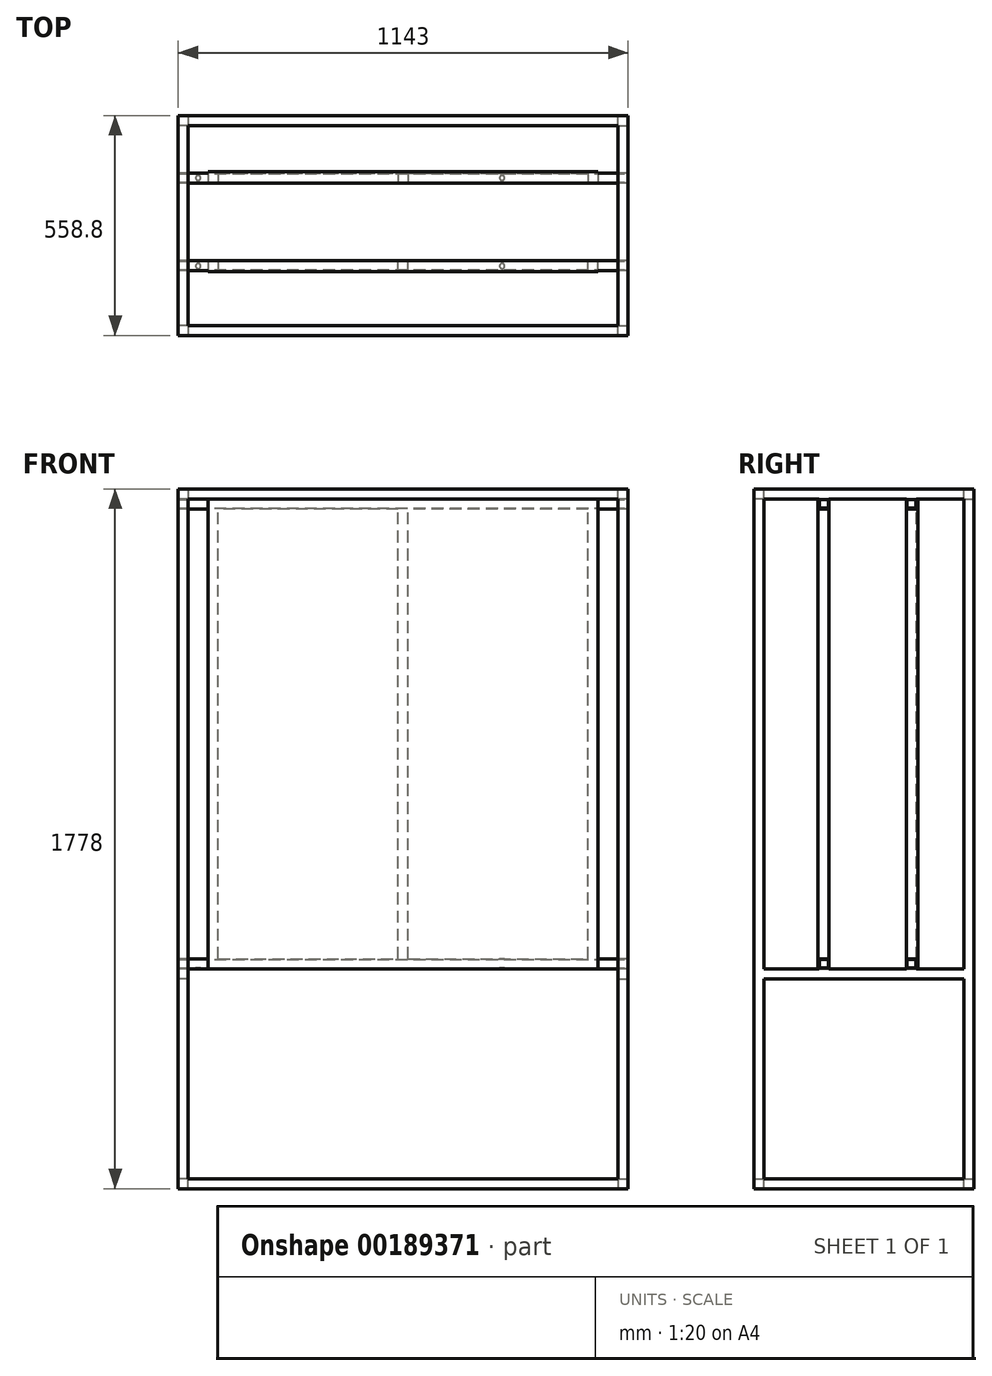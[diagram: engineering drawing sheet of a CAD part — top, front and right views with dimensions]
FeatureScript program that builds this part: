
annotation { "Feature Type Name" : "Feature", "Feature Type Description" : "" }
export const myFeature = defineFeature(function(context is Context, id is Id, definition is map)
    precondition{}
    {
        {
            var Q0;
            Q0=qCreatedBy(makeId("Front.planeOp"),FACE);
            var sketch = newSketch(context, id + "F0", { "sketchPlane" : qUnion([Q0])});
            skLineSegment(sketch, "E0.bottom", {"start": v(0, 0) * mm, "end": v(25.4, 0) * mm});
            skLineSegment(sketch, "E0.top", {"start": v(0, 25.4) * mm, "end": v(25.4, 25.4) * mm});
            skLineSegment(sketch, "E0.left", {"start": v(0, 0) * mm, "end": v(0, 25.4) * mm});
            skLineSegment(sketch, "E0.right", {"start": v(25.4, 0) * mm, "end": v(25.4, 25.4) * mm});
            skLineSegment(sketch, "E1.bottom", {"start": v(0, 533.4) * mm, "end": v(25.4, 533.4) * mm});
            skLineSegment(sketch, "E1.top", {"start": v(0, 558.8) * mm, "end": v(25.4, 558.8) * mm});
            skLineSegment(sketch, "E1.left", {"start": v(0, 533.4) * mm, "end": v(0, 558.8) * mm});
            skLineSegment(sketch, "E1.right", {"start": v(25.4, 533.4) * mm, "end": v(25.4, 558.8) * mm});
            skLineSegment(sketch, "E2.bottom", {"start": v(0, 1752.6) * mm, "end": v(25.4, 1752.6) * mm});
            skLineSegment(sketch, "E2.top", {"start": v(0, 1778) * mm, "end": v(25.4, 1778) * mm});
            skLineSegment(sketch, "E2.left", {"start": v(0, 1752.6) * mm, "end": v(0, 1778) * mm});
            skLineSegment(sketch, "E2.right", {"start": v(25.4, 1752.6) * mm, "end": v(25.4, 1778) * mm});
            skLineSegment(sketch, "E3", {"start": v(0, 25.4) * mm, "end": v(0, 558.8) * mm, "construction": true});
            skLineSegment(sketch, "E4.bottom", {"start": v(1117.6, 1778) * mm, "end": v(1143, 1778) * mm});
            skLineSegment(sketch, "E4.top", {"start": v(1117.6, 1752.6) * mm, "end": v(1143, 1752.6) * mm});
            skLineSegment(sketch, "E4.left", {"start": v(1117.6, 1778) * mm, "end": v(1117.6, 1752.6) * mm});
            skLineSegment(sketch, "E4.right", {"start": v(1143, 1778) * mm, "end": v(1143, 1752.6) * mm});
            skLineSegment(sketch, "E5.bottom", {"start": v(1117.6, 558.8) * mm, "end": v(1143, 558.8) * mm});
            skLineSegment(sketch, "E5.top", {"start": v(1117.6, 533.4) * mm, "end": v(1143, 533.4) * mm});
            skLineSegment(sketch, "E5.left", {"start": v(1117.6, 558.8) * mm, "end": v(1117.6, 533.4) * mm});
            skLineSegment(sketch, "E5.right", {"start": v(1143, 558.8) * mm, "end": v(1143, 533.4) * mm});
            skLineSegment(sketch, "E6.bottom", {"start": v(1117.6, 25.4) * mm, "end": v(1143, 25.4) * mm});
            skLineSegment(sketch, "E6.top", {"start": v(1117.6, 0) * mm, "end": v(1143, 0) * mm});
            skLineSegment(sketch, "E6.left", {"start": v(1117.6, 25.4) * mm, "end": v(1117.6, 0) * mm});
            skLineSegment(sketch, "E6.right", {"start": v(1143, 25.4) * mm, "end": v(1143, 0) * mm});
            skSolve(sketch);
        }
        {
            var Q0;
            Q0=qSketchRegion(id+"F0",true);
            extrude(context, id + "F1", {"entities" : qUnion([Q0]), "depth" : 558.8 * mm});
        }
        {
            var Q0;
            Q0=qCreatedBy(makeId("Right.planeOp"),FACE);
            var sketch = newSketch(context, id + "F2", { "sketchPlane" : qUnion([Q0])});
            skLineSegment(sketch, "E7.bottom", {"start": v(-558.8, 1752.6) * mm, "end": v(-533.4, 1752.6) * mm});
            skLineSegment(sketch, "E7.top", {"start": v(-558.8, 1778) * mm, "end": v(-533.4, 1778) * mm});
            skLineSegment(sketch, "E7.left", {"start": v(-558.8, 1778) * mm, "end": v(-558.8, 1752.6) * mm});
            skLineSegment(sketch, "E7.right", {"start": v(-533.4, 1778) * mm, "end": v(-533.4, 1752.6) * mm});
            skLineSegment(sketch, "E8.bottom", {"start": v(0, 1752.6) * mm, "end": v(-25.4, 1752.6) * mm});
            skLineSegment(sketch, "E8.top", {"start": v(0, 1778) * mm, "end": v(-25.4, 1778) * mm});
            skLineSegment(sketch, "E8.left", {"start": v(-25.4, 1778) * mm, "end": v(-25.4, 1752.6) * mm});
            skLineSegment(sketch, "E8.right", {"start": v(0, 1778) * mm, "end": v(0, 1752.6) * mm});
            skLineSegment(sketch, "E9.bottom", {"start": v(-558.8, 0) * mm, "end": v(-533.4, 0) * mm});
            skLineSegment(sketch, "E9.top", {"start": v(-558.8, 25.4) * mm, "end": v(-533.4, 25.4) * mm});
            skLineSegment(sketch, "E9.left", {"start": v(-558.8, 0) * mm, "end": v(-558.8, 25.4) * mm});
            skLineSegment(sketch, "E9.right", {"start": v(-533.4, 0) * mm, "end": v(-533.4, 25.4) * mm});
            skLineSegment(sketch, "E10.bottom", {"start": v(0, 0) * mm, "end": v(-25.4, 0) * mm});
            skLineSegment(sketch, "E10.top", {"start": v(0, 25.4) * mm, "end": v(-25.4, 25.4) * mm});
            skLineSegment(sketch, "E10.left", {"start": v(-25.4, 0) * mm, "end": v(-25.4, 25.4) * mm});
            skLineSegment(sketch, "E10.right", {"start": v(0, 0) * mm, "end": v(0, 25.4) * mm});
            skLineSegment(sketch, "E11.bottom", {"start": v(-393.7, 1752.6) * mm, "end": v(-368.3, 1752.6) * mm});
            skLineSegment(sketch, "E11.top", {"start": v(-393.7, 1727.2) * mm, "end": v(-368.3, 1727.2) * mm});
            skLineSegment(sketch, "E11.left", {"start": v(-393.7, 1752.6) * mm, "end": v(-393.7, 1727.2) * mm});
            skLineSegment(sketch, "E11.right", {"start": v(-368.3, 1752.6) * mm, "end": v(-368.3, 1727.2) * mm});
            skLineSegment(sketch, "E12.bottom", {"start": v(-171.45, 1752.6) * mm, "end": v(-146.05, 1752.6) * mm});
            skLineSegment(sketch, "E12.top", {"start": v(-171.45, 1727.2) * mm, "end": v(-146.05, 1727.2) * mm});
            skLineSegment(sketch, "E12.left", {"start": v(-171.45, 1752.6) * mm, "end": v(-171.45, 1727.2) * mm});
            skLineSegment(sketch, "E12.right", {"start": v(-146.05, 1752.6) * mm, "end": v(-146.05, 1727.2) * mm});
            skLineSegment(sketch, "E13.bottom", {"start": v(-393.7, 584.2) * mm, "end": v(-368.3, 584.2) * mm});
            skLineSegment(sketch, "E13.top", {"start": v(-393.7, 558.8) * mm, "end": v(-368.3, 558.8) * mm});
            skLineSegment(sketch, "E13.left", {"start": v(-393.7, 584.2) * mm, "end": v(-393.7, 558.8) * mm});
            skLineSegment(sketch, "E13.right", {"start": v(-368.3, 584.2) * mm, "end": v(-368.3, 558.8) * mm});
            skLineSegment(sketch, "E14.bottom", {"start": v(-146.05, 558.8) * mm, "end": v(-171.45, 558.8) * mm});
            skLineSegment(sketch, "E14.top", {"start": v(-146.05, 584.2) * mm, "end": v(-171.45, 584.2) * mm});
            skLineSegment(sketch, "E14.left", {"start": v(-146.05, 558.8) * mm, "end": v(-146.05, 584.2) * mm});
            skLineSegment(sketch, "E14.right", {"start": v(-171.45, 558.8) * mm, "end": v(-171.45, 584.2) * mm});
            skSolve(sketch);
        }
        {
            var Q0;
            Q0=qSketchRegion(id+"F2",true);
            var Q1;
            Q1=makeQuery(id+"F1.opExtrude","SWEPT_FACE",FACE,{"disambiguationData":[OSD([sQuery(id+"F0.wireOp",EDGE,"E4.right")])]});
            extrude(context, id + "F3", {"entities" : qUnion([Q0]), "operationType" : NewBodyOperationType.ADD, "endBound" : BoundingType.UP_TO_SURFACE, "endBoundEntityFace" : qUnion([Q1]), "depth" : 25.4 * mm});
        }
        {
            var Q0;
            Q0=qCreatedBy(makeId("Top.planeOp"),FACE);
            var sketch = newSketch(context, id + "F4", { "sketchPlane" : qUnion([Q0])});
            skLineSegment(sketch, "E15.bottom", {"start": v(0, 0) * mm, "end": v(25.4, 0) * mm});
            skLineSegment(sketch, "E15.top", {"start": v(0, -25.4) * mm, "end": v(25.4, -25.4) * mm});
            skLineSegment(sketch, "E15.left", {"start": v(0, 0) * mm, "end": v(0, -25.4) * mm});
            skLineSegment(sketch, "E15.right", {"start": v(25.4, 0) * mm, "end": v(25.4, -25.4) * mm});
            skLineSegment(sketch, "E16.bottom", {"start": v(1143, 0) * mm, "end": v(1117.6, 0) * mm});
            skLineSegment(sketch, "E16.top", {"start": v(1143, -25.4) * mm, "end": v(1117.6, -25.4) * mm});
            skLineSegment(sketch, "E16.left", {"start": v(1143, 0) * mm, "end": v(1143, -25.4) * mm});
            skLineSegment(sketch, "E16.right", {"start": v(1117.6, 0) * mm, "end": v(1117.6, -25.4) * mm});
            skLineSegment(sketch, "E17.bottom", {"start": v(0, -558.8) * mm, "end": v(25.4, -558.8) * mm});
            skLineSegment(sketch, "E17.top", {"start": v(0, -533.4) * mm, "end": v(25.4, -533.4) * mm});
            skLineSegment(sketch, "E17.left", {"start": v(0, -558.8) * mm, "end": v(0, -533.4) * mm});
            skLineSegment(sketch, "E17.right", {"start": v(25.4, -558.8) * mm, "end": v(25.4, -533.4) * mm});
            skLineSegment(sketch, "E18.bottom", {"start": v(1143, -558.8) * mm, "end": v(1117.6, -558.8) * mm});
            skLineSegment(sketch, "E18.top", {"start": v(1143, -533.4) * mm, "end": v(1117.6, -533.4) * mm});
            skLineSegment(sketch, "E18.left", {"start": v(1143, -558.8) * mm, "end": v(1143, -533.4) * mm});
            skLineSegment(sketch, "E18.right", {"start": v(1117.6, -558.8) * mm, "end": v(1117.6, -533.4) * mm});
            skSolve(sketch);
        }
        {
            var Q0;
            Q0=qSketchRegion(id+"F4",true);
            var Q1;
            Q1=makeQuery(id+"F3.boolean.opBoolean","MERGE",FACE,{"derivedFrom":[makeQuery(id+"F1.opExtrude","SWEPT_FACE",FACE,{"disambiguationData":[OSD([sQuery(id+"F0.wireOp",EDGE,"E2.top")])]}),makeQuery(id+"F1.opExtrude","SWEPT_FACE",FACE,{"disambiguationData":[OSD([sQuery(id+"F0.wireOp",EDGE,"E4.bottom")])]}),makeQuery(id+"F1.opExtrude","SWEPT_FACE",FACE,{"disambiguationData":[OSD([sQuery(id+"F0.wireOp",EDGE,"0Fs5lVdm-4J5u-nsDr-3WOj-KorWAGg2DyWV.bottom")])]}),makeQuery(id+"F3.opExtrude","SWEPT_FACE",FACE,{"disambiguationData":[OSD([sQuery(id+"F2.wireOp",EDGE,"E7.top")])]}),makeQuery(id+"F3.opExtrude","SWEPT_FACE",FACE,{"disambiguationData":[OSD([sQuery(id+"F2.wireOp",EDGE,"E8.top")])]})]});
            extrude(context, id + "F5", {"entities" : qUnion([Q0]), "operationType" : NewBodyOperationType.ADD, "endBound" : BoundingType.UP_TO_SURFACE, "endBoundEntityFace" : qUnion([Q1]), "depth" : 25.4 * mm});
        }
        {
            var Q0;
            Q0=makeQuery(id+"F3.opExtrude","SWEPT_FACE",FACE,{"disambiguationData":[OSD([sQuery(id+"F2.wireOp",EDGE,"E11.left")])]});
            var sketch = newSketch(context, id + "F6", { "sketchPlane" : qUnion([Q0])});
            skLineSegment(sketch, "E19.bottom", {"start": v(76.2, 1752.6) * mm, "end": v(1066.8, 1752.6) * mm});
            skLineSegment(sketch, "E19.top", {"start": v(76.2, 558.8) * mm, "end": v(1066.8, 558.8) * mm});
            skLineSegment(sketch, "E19.left", {"start": v(76.2, 1752.6) * mm, "end": v(76.2, 558.8) * mm});
            skLineSegment(sketch, "E19.right", {"start": v(1066.8, 1752.6) * mm, "end": v(1066.8, 558.8) * mm});
            skSolve(sketch);
        }
        {
            var Q0;
            Q0=qSketchRegion(id+"F6",true);
            var Q1;
            Q1=makeQuery(id+"F5.boolean.opBoolean","MERGE",FACE,{"derivedFrom":[makeQuery(id+"F1.opExtrude","SWEPT_FACE",FACE,{"disambiguationData":[OSD([sQuery(id+"F0.wireOp",EDGE,"0Fs5lVdm-4J5u-nsDr-3WOj-KorWAGg2DyWV.left")])]}),makeQuery(id+"F1.opExtrude","SWEPT_FACE",FACE,{"disambiguationData":[OSD([sQuery(id+"F0.wireOp",EDGE,"EeBZonoS-u3Hg-k4z5-gOjs-0P7sHEG4NNOG.left")])]}),makeQuery(id+"F5.opExtrude","SWEPT_FACE",FACE,{"disambiguationData":[OSD([sQuery(id+"F4.wireOp",EDGE,"BKoOxQ88-9Bi7-qn13-0Goz-K5id2RvQMVBP.left")])]}),makeQuery(id+"F5.opExtrude","SWEPT_FACE",FACE,{"disambiguationData":[OSD([sQuery(id+"F4.wireOp",EDGE,"BeZ8DR4E-C6G6-KDQH-JixA-5zQBHozv28L4.left")])]})]});
            extrude(context, id + "F7", {"entities" : qUnion([Q0]), "endBoundEntityFace" : qUnion([Q1]), "depth" : 3.05 * mm});
        }
        {
            var Q0;
            Q0=makeQuery(id+"F3.opExtrude","SWEPT_FACE",FACE,{"disambiguationData":[OSD([sQuery(id+"F2.wireOp",EDGE,"E12.right")])]});
            var sketch = newSketch(context, id + "F8", { "sketchPlane" : qUnion([Q0])});
            skLineSegment(sketch, "E20.0", {"start": v(-76.2, 1752.6) * mm, "end": v(-1066.8, 1752.6) * mm});
            skLineSegment(sketch, "E20.1", {"start": v(-76.2, 558.8) * mm, "end": v(-1066.8, 558.8) * mm});
            skLineSegment(sketch, "E20.2", {"start": v(-76.2, 1752.6) * mm, "end": v(-76.2, 558.8) * mm});
            skLineSegment(sketch, "E20.3", {"start": v(-1066.8, 1752.6) * mm, "end": v(-1066.8, 558.8) * mm});
            skSolve(sketch);
        }
        {
            var Q0;
            Q0 = qSketchRegion(id + "F8", true);
            extrude(context, id + "F9", {"entities" : qUnion([Q0]), "depth" : 3.05 * mm});
        }
        {
            var Q0;
            {var subQ0=sQuery(id+"F0.wireOp",EDGE,"E4.right");Q0=makeQuery(id+"F5.boolean.opBoolean","MERGE",FACE,{"derivedFrom":[makeQuery(id+"F3.boolean.opBoolean","MERGE",FACE,{"derivedFrom":[makeQuery(id+"F1.opExtrude","SWEPT_FACE",FACE,{"disambiguationData":[OSD([subQ0])]}),makeQuery(id+"F3.opExtrude","CAP_FACE",FACE,{"disambiguationData":[OSD([subQ0]),ownerDisambiguation([makeQuery(id+"F3.opExtrude","SWEPT_BODY",BODY,{"disambiguationData":[OSD([sQuery(id+"F2.wireOp",EDGE,"E11.bottom"),sQuery(id+"F2.wireOp",EDGE,"E11.top"),sQuery(id+"F2.wireOp",EDGE,"E11.left"),sQuery(id+"F2.wireOp",EDGE,"E11.right")])]})])],"isStart":false}),makeQuery(id+"F3.opExtrude","CAP_FACE",FACE,{"disambiguationData":[OSD([subQ0]),ownerDisambiguation([makeQuery(id+"F3.opExtrude","SWEPT_BODY",BODY,{"disambiguationData":[OSD([sQuery(id+"F2.wireOp",EDGE,"E12.bottom"),sQuery(id+"F2.wireOp",EDGE,"E12.top"),sQuery(id+"F2.wireOp",EDGE,"E12.left"),sQuery(id+"F2.wireOp",EDGE,"E12.right")])]})])],"isStart":false})]}),makeQuery(id+"F3.boolean.opBoolean","MERGE",FACE,{"derivedFrom":[makeQuery(id+"F1.opExtrude","SWEPT_FACE",FACE,{"disambiguationData":[OSD([sQuery(id+"F0.wireOp",EDGE,"E5.right")])]}),makeQuery(id+"F3.opExtrude","CAP_FACE",FACE,{"disambiguationData":[OSD([subQ0]),ownerDisambiguation([makeQuery(id+"F3.opExtrude","SWEPT_BODY",BODY,{"disambiguationData":[OSD([sQuery(id+"F2.wireOp",EDGE,"E13.bottom"),sQuery(id+"F2.wireOp",EDGE,"E13.top"),sQuery(id+"F2.wireOp",EDGE,"E13.left"),sQuery(id+"F2.wireOp",EDGE,"E13.right")])]})])],"isStart":false}),makeQuery(id+"F3.opExtrude","CAP_FACE",FACE,{"disambiguationData":[OSD([subQ0]),ownerDisambiguation([makeQuery(id+"F3.opExtrude","SWEPT_BODY",BODY,{"disambiguationData":[OSD([sQuery(id+"F2.wireOp",EDGE,"E14.bottom"),sQuery(id+"F2.wireOp",EDGE,"E14.top"),sQuery(id+"F2.wireOp",EDGE,"E14.left"),sQuery(id+"F2.wireOp",EDGE,"E14.right")])]})])],"isStart":false})]}),makeQuery(id+"F1.opExtrude","SWEPT_FACE",FACE,{"disambiguationData":[OSD([sQuery(id+"F0.wireOp",EDGE,"E6.right")])]}),makeQuery(id+"F5.opExtrude","SWEPT_FACE",FACE,{"disambiguationData":[OSD([sQuery(id+"F4.wireOp",EDGE,"E16.left")])]}),makeQuery(id+"F5.opExtrude","SWEPT_FACE",FACE,{"disambiguationData":[OSD([sQuery(id+"F4.wireOp",EDGE,"E18.left")])]})]});}
            var sketch = newSketch(context, id + "F10", { "sketchPlane" : qUnion([Q0])});
            skLineSegment(sketch, "E21.0", {"start": v(-369.82, 1751.08) * mm, "end": v(-369.82, 1728.72) * mm});
            skLineSegment(sketch, "E21.1", {"start": v(-392.18, 1728.72) * mm, "end": v(-369.82, 1728.72) * mm});
            skLineSegment(sketch, "E21.2", {"start": v(-392.18, 1751.08) * mm, "end": v(-392.18, 1728.72) * mm});
            skLineSegment(sketch, "E22", {"start": v(-392.18, 1751.08) * mm, "end": v(-369.82, 1751.08) * mm});
            skLineSegment(sketch, "E23.0", {"start": v(-147.57, 1751.08) * mm, "end": v(-147.57, 1728.72) * mm});
            skLineSegment(sketch, "E23.1", {"start": v(-169.93, 1728.72) * mm, "end": v(-147.57, 1728.72) * mm});
            skLineSegment(sketch, "E23.2", {"start": v(-169.93, 1751.08) * mm, "end": v(-169.93, 1728.72) * mm});
            skLineSegment(sketch, "E24.0", {"start": v(-565.15, -6.35) * mm, "end": v(6.35, -6.35) * mm});
            skLineSegment(sketch, "E24.1", {"start": v(-565.15, 1784.35) * mm, "end": v(-565.15, -6.35) * mm});
            skLineSegment(sketch, "E24.2", {"start": v(6.35, 1784.35) * mm, "end": v(-565.15, 1784.35) * mm});
            skLineSegment(sketch, "E24.3", {"start": v(6.35, -6.35) * mm, "end": v(6.35, 1784.35) * mm});
            skLineSegment(sketch, "E25", {"start": v(-169.93, 1751.08) * mm, "end": v(-147.57, 1751.08) * mm});
            skLineSegment(sketch, "E26.bottom", {"start": v(-392.18, 582.68) * mm, "end": v(-369.82, 582.68) * mm});
            skLineSegment(sketch, "E26.top", {"start": v(-392.18, 560.32) * mm, "end": v(-369.82, 560.32) * mm});
            skLineSegment(sketch, "E26.left", {"start": v(-392.18, 582.68) * mm, "end": v(-392.18, 560.32) * mm});
            skLineSegment(sketch, "E26.right", {"start": v(-369.82, 582.68) * mm, "end": v(-369.82, 560.32) * mm});
            skLineSegment(sketch, "E27.bottom", {"start": v(-147.57, 560.32) * mm, "end": v(-169.93, 560.32) * mm});
            skLineSegment(sketch, "E27.top", {"start": v(-147.57, 582.68) * mm, "end": v(-169.93, 582.68) * mm});
            skLineSegment(sketch, "E27.left", {"start": v(-147.57, 560.32) * mm, "end": v(-147.57, 582.68) * mm});
            skLineSegment(sketch, "E27.right", {"start": v(-169.93, 560.32) * mm, "end": v(-169.93, 582.68) * mm});
            skSolve(sketch);
        }
        {
            var Q0;
            Q0=makeQuery(id+"F10.imprint","IMPRINT",FACE,{"disambiguationData":[TD([[makeQuery(id+"F10.imprint","IMPRINT",EDGE,{"derivedFrom":sQuery(id+"F10.wireOp",EDGE,"E27.bottom")}),-1.0]])]});
            var Q1;
            Q1=makeQuery(id+"F10.imprint","IMPRINT",FACE,{"disambiguationData":[TD([[makeQuery(id+"F10.imprint","IMPRINT",EDGE,{"derivedFrom":sQuery(id+"F10.wireOp",EDGE,"E26.bottom")}),-1.0]])]});
            var Q2;
            Q2=makeQuery(id+"F10.imprint","IMPRINT",FACE,{"disambiguationData":[TD([[makeQuery(id+"F10.imprint","IMPRINT",EDGE,{"derivedFrom":sQuery(id+"F10.wireOp",EDGE,"E21.0")}),-1.0]])]});
            var Q3;
            Q3=makeQuery(id+"F10.imprint","IMPRINT",FACE,{"disambiguationData":[TD([[makeQuery(id+"F10.imprint","IMPRINT",EDGE,{"derivedFrom":sQuery(id+"F10.wireOp",EDGE,"E23.0")}),-1.0]])]});
            var Q4;
            Q4=makeQuery(id+"F10.imprint","IMPRINT",FACE,{"disambiguationData":[TD([[makeQuery(id+"F10.imprint","IMPRINT",EDGE,{"derivedFrom":sQuery(id+"F10.wireOp",EDGE,"zKFJQELe-OJ9g-ilxq-14OP-r4SHmfK5YD3d.bottom")}),-1.0]])]});
            var Q5;
            Q5=makeQuery(id+"F10.imprint","IMPRINT",FACE,{"disambiguationData":[TD([[makeQuery(id+"F10.imprint","IMPRINT",EDGE,{"derivedFrom":sQuery(id+"F10.wireOp",EDGE,"MuMn5QwJ-G6kR-dJPt-m1Qy-jcOfBHaSi1D3.bottom")}),-1.0]])]});
            extrude(context, id + "F11", {"entities" : qUnion([Q0, Q1, Q2, Q3, Q4, Q5]), "operationType" : NewBodyOperationType.REMOVE, "endBound" : BoundingType.THROUGH_ALL, "oppositeDirection" : true, "depth" : 25.4 * mm});
        }
        {
            var Q0;
            Q0=makeQuery(id+"F3.opExtrude","SWEPT_FACE",FACE,{"disambiguationData":[OSD([sQuery(id+"F2.wireOp",EDGE,"E13.bottom")])]});
            var sketch = newSketch(context, id + "F12", { "sketchPlane" : qUnion([Q0])});
            skLineSegment(sketch, "E28.bottom", {"start": v(50.8, -158.75) * mm, "end": v(822.96, -158.75) * mm, "construction": true});
            skLineSegment(sketch, "E28.top", {"start": v(50.8, -382.78) * mm, "end": v(822.96, -382.78) * mm, "construction": true});
            skLineSegment(sketch, "E28.left", {"start": v(50.8, -158.75) * mm, "end": v(50.8, -382.78) * mm, "construction": true});
            skLineSegment(sketch, "E28.right", {"start": v(822.96, -158.75) * mm, "end": v(822.96, -382.78) * mm, "construction": true});
            skCircle(sketch, "E29", {"center": v(50.8, -158.75) * mm, "radius": 6.35 * mm});
            skCircle(sketch, "E30", {"center": v(50.8, -382.78) * mm, "radius": 6.35 * mm});
            skCircle(sketch, "E31", {"center": v(822.96, -382.78) * mm, "radius": 6.35 * mm});
            skCircle(sketch, "E32", {"center": v(822.96, -158.75) * mm, "radius": 6.35 * mm});
            skSolve(sketch);
        }
        {
            var Q0;
            Q0 = qSketchRegion(id + "F12", true);
            extrude(context, id + "F13", {"entities" : qUnion([Q0]), "operationType" : NewBodyOperationType.REMOVE, "endBound" : BoundingType.THROUGH_ALL, "oppositeDirection" : true, "depth" : 25.4 * mm});
        }
        {
            var Q0;
            Q0=makeQuery(id+"F3.opExtrude","SWEPT_FACE",FACE,{"disambiguationData":[OSD([sQuery(id+"F2.wireOp",EDGE,"E11.top")])]});
            var sketch = newSketch(context, id + "F14", { "sketchPlane" : qUnion([Q0])});
            skLineSegment(sketch, "E33.bottom", {"start": v(76.2, 146.05) * mm, "end": v(101.6, 146.05) * mm});
            skLineSegment(sketch, "E33.top", {"start": v(76.2, 171.45) * mm, "end": v(101.6, 171.45) * mm});
            skLineSegment(sketch, "E33.left", {"start": v(76.2, 146.05) * mm, "end": v(76.2, 171.45) * mm});
            skLineSegment(sketch, "E33.right", {"start": v(101.6, 146.05) * mm, "end": v(101.6, 171.45) * mm});
            skPoint(sketch, "E34.oppositeSnap0", {"position": v(88.9, 171.45) * mm});
            skLineSegment(sketch, "E34.bottom", {"start": v(1066.8, 146.05) * mm, "end": v(1041.4, 146.05) * mm});
            skLineSegment(sketch, "E34.top", {"start": v(1066.8, 171.45) * mm, "end": v(1041.4, 171.45) * mm});
            skLineSegment(sketch, "E34.left", {"start": v(1066.8, 146.05) * mm, "end": v(1066.8, 171.45) * mm});
            skLineSegment(sketch, "E34.right", {"start": v(1041.4, 146.05) * mm, "end": v(1041.4, 171.45) * mm});
            skLineSegment(sketch, "E35.bottom", {"start": v(1066.8, 393.7) * mm, "end": v(1041.4, 393.7) * mm});
            skLineSegment(sketch, "E35.top", {"start": v(1066.8, 368.3) * mm, "end": v(1041.4, 368.3) * mm});
            skLineSegment(sketch, "E35.left", {"start": v(1066.8, 393.7) * mm, "end": v(1066.8, 368.3) * mm});
            skLineSegment(sketch, "E35.right", {"start": v(1041.4, 393.7) * mm, "end": v(1041.4, 368.3) * mm});
            skLineSegment(sketch, "E36.bottom", {"start": v(76.2, 368.3) * mm, "end": v(101.6, 368.3) * mm});
            skLineSegment(sketch, "E36.top", {"start": v(76.2, 393.7) * mm, "end": v(101.6, 393.7) * mm});
            skLineSegment(sketch, "E36.left", {"start": v(76.2, 368.3) * mm, "end": v(76.2, 393.7) * mm});
            skLineSegment(sketch, "E36.right", {"start": v(101.6, 368.3) * mm, "end": v(101.6, 393.7) * mm});
            skLineSegment(sketch, "E37.bottom", {"start": v(558.8, 146.05) * mm, "end": v(584.2, 146.05) * mm});
            skLineSegment(sketch, "E37.top", {"start": v(558.8, 171.45) * mm, "end": v(584.2, 171.45) * mm});
            skLineSegment(sketch, "E37.left", {"start": v(558.8, 146.05) * mm, "end": v(558.8, 171.45) * mm});
            skLineSegment(sketch, "E37.right", {"start": v(584.2, 146.05) * mm, "end": v(584.2, 171.45) * mm});
            skLineSegment(sketch, "E38.bottom", {"start": v(558.8, 393.7) * mm, "end": v(584.2, 393.7) * mm});
            skLineSegment(sketch, "E38.top", {"start": v(558.8, 368.3) * mm, "end": v(584.2, 368.3) * mm});
            skLineSegment(sketch, "E38.left", {"start": v(558.8, 393.7) * mm, "end": v(558.8, 368.3) * mm});
            skLineSegment(sketch, "E38.right", {"start": v(584.2, 393.7) * mm, "end": v(584.2, 368.3) * mm});
            skLineSegment(sketch, "E39", {"start": v(101.6, 171.45) * mm, "end": v(558.8, 171.45) * mm, "construction": true});
            skLineSegment(sketch, "E40", {"start": v(584.2, 171.45) * mm, "end": v(1041.4, 171.45) * mm, "construction": true});
            skSolve(sketch);
        }
        {
            var Q0;
            Q0 = qSketchRegion(id + "F14", true);
            var Q1;
            Q1=makeQuery(id+"F3.opExtrude","SWEPT_FACE",FACE,{"disambiguationData":[OSD([sQuery(id+"F2.wireOp",EDGE,"E14.top")])]});
            extrude(context, id + "F15", {"entities" : qUnion([Q0]), "operationType" : NewBodyOperationType.ADD, "endBound" : BoundingType.UP_TO_SURFACE, "endBoundEntityFace" : qUnion([Q1]), "depth" : 25.4 * mm});
        }
    });
